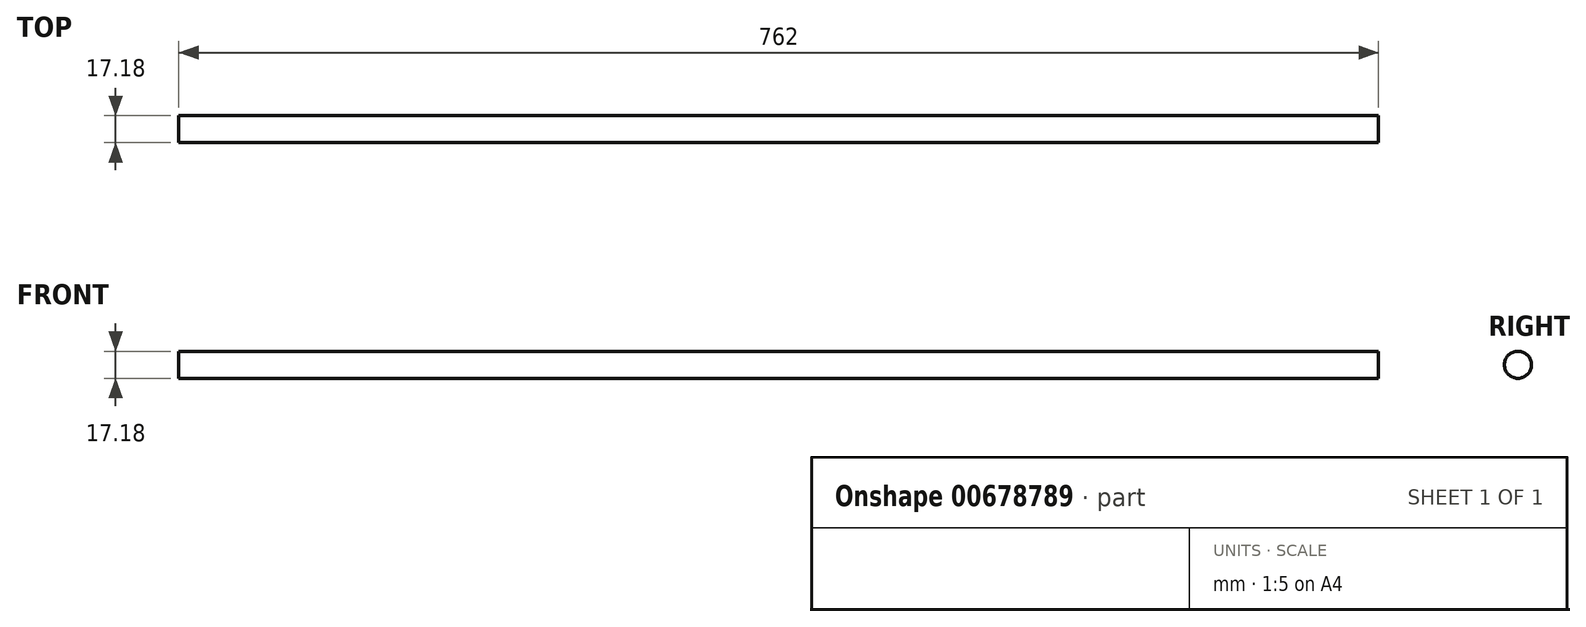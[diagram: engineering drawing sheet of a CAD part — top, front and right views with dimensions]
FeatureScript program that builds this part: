
annotation { "Feature Type Name" : "Feature", "Feature Type Description" : "" }
export const myFeature = defineFeature(function(context is Context, id is Id, definition is map)
    precondition{}
    {
        {
            var Q0;
            Q0=qCreatedBy(makeId("Right.planeOp"),FACE);
            var sketch = newSketch(context, id + "F0", { "sketchPlane" : qUnion([Q0])});
            skCircle(sketch, "E0", {"center": v(0, 0) * mm, "radius": 59.65 * mm});
            skSolve(sketch);
        }
        {
            var Q0;
            Q0=makeQuery(id+"F0.imprint","IMPRINT",FACE,{"disambiguationData":[TD([[makeQuery(id+"F0.imprint","IMPRINT",EDGE,{"derivedFrom":sQuery(id+"F0.wireOp",EDGE,"E0")}),1.0]])]});
            extrude(context, id + "F1", {"entities" : qUnion([Q0]), "depth" : 304.8 * mm, "offsetDistance" : 25.4 * mm, "hasSecondDirection" : true, "secondDirectionOppositeDirection" : true, "secondDirectionDepth" : 304.8 * mm});
        }
        {
            var Q0;
            Q0=makeQuery(id+"F1.opExtrude","CAP_FACE",FACE,{"disambiguationData":[OSD([sQuery(id+"F0.wireOp",EDGE,"E0")])],"isStart":false});
            var sketch = newSketch(context, id + "F2", { "sketchPlane" : qUnion([Q0])});
            skCircle(sketch, "E1", {"center": v(0, 0) * mm, "radius": 21.07 * mm});
            skSolve(sketch);
        }
        {
            var Q0;
            Q0=makeQuery(id+"F2.imprint","IMPRINT",FACE,{"disambiguationData":[TD([[makeQuery(id+"F2.imprint","IMPRINT",EDGE,{"derivedFrom":sQuery(id+"F2.wireOp",EDGE,"E1")}),-1.0]])]});
            extrude(context, id + "F3", {"entities" : qUnion([Q0]), "operationType" : NewBodyOperationType.REMOVE, "endBound" : BoundingType.THROUGH_ALL, "oppositeDirection" : true, "depth" : 25.4 * mm, "offsetDistance" : 25.4 * mm});
        }
        {
            var Q0;
            Q0=makeQuery(id+"F1.opExtrude","CAP_FACE",FACE,{"disambiguationData":[OSD([sQuery(id+"F0.wireOp",EDGE,"E0")])],"isStart":false});
            var sketch = newSketch(context, id + "F4", { "sketchPlane" : qUnion([Q0])});
            skCircle(sketch, "E2", {"center": v(0, 0) * mm, "radius": 8.59 * mm});
            skSolve(sketch);
        }
        {
            var Q0;
            Q0=makeQuery(id+"F4.imprint","IMPRINT",FACE,{"disambiguationData":[TD([[makeQuery(id+"F4.imprint","IMPRINT",EDGE,{"derivedFrom":sQuery(id+"F4.wireOp",EDGE,"E2")}),-1.0]])]});
            extrude(context, id + "F5", {"entities" : qUnion([Q0]), "operationType" : NewBodyOperationType.REMOVE, "endBound" : BoundingType.THROUGH_ALL, "oppositeDirection" : true, "depth" : 25.4 * mm, "offsetDistance" : 25.4 * mm});
        }
        {
            var Q0;
            Q0=makeQuery(id+"F1.opExtrude","CAP_FACE",FACE,{"disambiguationData":[OSD([sQuery(id+"F0.wireOp",EDGE,"E0")])],"isStart":false});
            extrude(context, id + "F6", {"entities" : qUnion([Q0]), "operationType" : NewBodyOperationType.ADD, "depth" : 152.4 * mm, "offsetDistance" : 25.4 * mm});
        }
        {
            var Q0;
            Q0=makeQuery(id+"F1.opExtrude","CAP_FACE",FACE,{"disambiguationData":[OSD([sQuery(id+"F0.wireOp",EDGE,"E0")])],"isStart":true});
            extrude(context, id + "F7", {"entities" : qUnion([Q0]), "operationType" : NewBodyOperationType.ADD, "depth" : 152.4 * mm, "offsetDistance" : 25.4 * mm});
        }
        {
            var Q0;
            Q0=makeQuery(id+"F6.opExtrude","CAP_FACE",FACE,{"disambiguationData":[OSD([sQuery(id+"F0.wireOp",EDGE,"E0")])],"isStart":false});
            extrude(context, id + "F8", {"entities" : qUnion([Q0]), "operationType" : NewBodyOperationType.REMOVE, "oppositeDirection" : true, "depth" : 76.2 * mm, "offsetDistance" : 25.4 * mm});
        }
        {
            var Q0;
            Q0=makeQuery(id+"F7.opExtrude","CAP_FACE",FACE,{"disambiguationData":[OSD([sQuery(id+"F0.wireOp",EDGE,"E0")])],"isStart":false});
            extrude(context, id + "F9", {"entities" : qUnion([Q0]), "operationType" : NewBodyOperationType.REMOVE, "oppositeDirection" : true, "depth" : 76.2 * mm, "offsetDistance" : 25.4 * mm});
        }
    });
